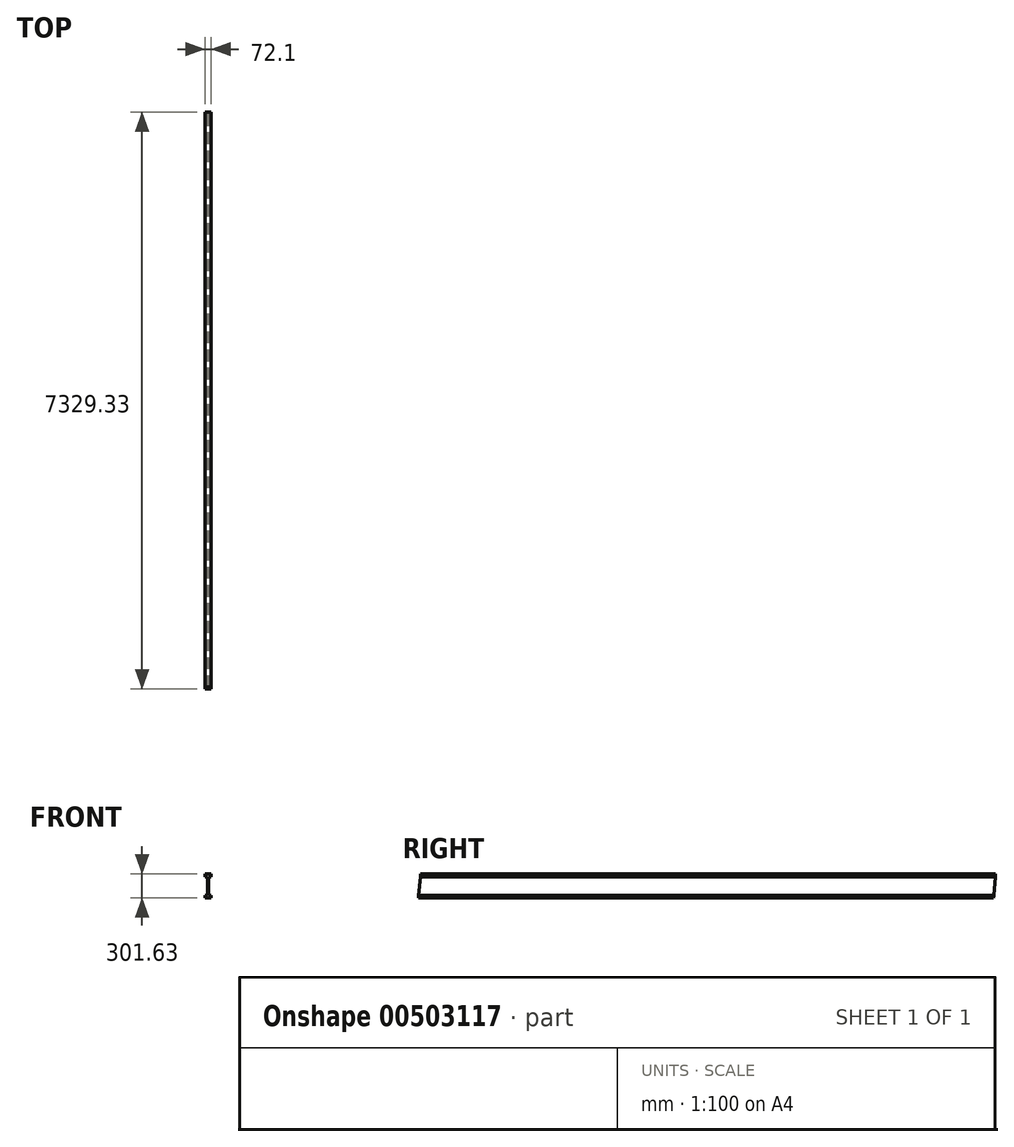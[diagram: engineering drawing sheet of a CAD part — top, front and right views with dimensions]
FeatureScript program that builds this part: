
annotation { "Feature Type Name" : "Feature", "Feature Type Description" : "" }
export const myFeature = defineFeature(function(context is Context, id is Id, definition is map)
    precondition{}
    {
        {
            var Q0;
            Q0=qCreatedBy(makeId("Front.planeOp"),FACE);
            var sketch = newSketch(context, id + "F0", { "sketchPlane" : qUnion([Q0])});
            skLineSegment(sketch, "E0", {"start": v(0, 0) * mm, "end": v(0, 33.65) * mm});
            skLineSegment(sketch, "E1", {"start": v(0, 33.65) * mm, "end": v(31.29, 33.65) * mm});
            skLineSegment(sketch, "E2", {"start": v(31.29, 33.65) * mm, "end": v(31.29, 267.97) * mm});
            skLineSegment(sketch, "E3", {"start": v(31.29, 267.97) * mm, "end": v(0, 267.97) * mm});
            skLineSegment(sketch, "E4", {"start": v(0, 267.97) * mm, "end": v(0, 301.63) * mm});
            skLineSegment(sketch, "E5", {"start": v(0, 301.63) * mm, "end": v(72.1, 301.63) * mm});
            skLineSegment(sketch, "E6", {"start": v(72.1, 301.63) * mm, "end": v(72.1, 267.97) * mm});
            skLineSegment(sketch, "E7", {"start": v(72.1, 267.97) * mm, "end": v(40.81, 267.97) * mm});
            skLineSegment(sketch, "E8", {"start": v(40.81, 267.97) * mm, "end": v(40.81, 33.65) * mm});
            skLineSegment(sketch, "E9", {"start": v(40.81, 33.65) * mm, "end": v(72.1, 33.66) * mm});
            skLineSegment(sketch, "E10", {"start": v(72.1, 33.66) * mm, "end": v(72.1, 0) * mm});
            skLineSegment(sketch, "E11", {"start": v(72.1, 0) * mm, "end": v(0, 0) * mm});
            skSolve(sketch);
        }
        {
            var Q0;
            Q0 = qSketchRegion(id + "F0", true);
            extrude(context, id + "F1", {"entities" : qUnion([Q0]), "depth" : 7620 * mm});
        }
        {
            var Q0;
            Q0=makeQuery(id+"F1.opExtrude","SWEPT_FACE",FACE,{"disambiguationData":[OSD([sQuery(id+"F0.wireOp",EDGE,"E10")])]});
            var sketch = newSketch(context, id + "F2", { "sketchPlane" : qUnion([Q0])});
            skLineSegment(sketch, "E12", {"start": v(-7620, 0) * mm, "end": v(-7594.25, 301.63) * mm});
            skLineSegment(sketch, "E13", {"start": v(-7620, 0) * mm, "end": v(-7620, 301.63) * mm});
            skLineSegment(sketch, "E14", {"start": v(-7620, 301.63) * mm, "end": v(-7594.25, 301.63) * mm});
            skSolve(sketch);
        }
        {
            var Q0;
            Q0 = qSketchRegion(id + "F2", true);
            extrude(context, id + "F3", {"entities" : qUnion([Q0]), "operationType" : NewBodyOperationType.REMOVE, "endBound" : BoundingType.THROUGH_ALL, "oppositeDirection" : true, "depth" : 25.4 * mm});
        }
        {
            var Q0;
            Q0=makeQuery(id+"F1.opExtrude","SWEPT_FACE",FACE,{"disambiguationData":[OSD([sQuery(id+"F0.wireOp",EDGE,"E0")])]});
            var sketch = newSketch(context, id + "F4", { "sketchPlane" : qUnion([Q0])});
            skLineSegment(sketch, "E15", {"start": v(316.42, 0) * mm, "end": v(290.67, 301.63) * mm});
            skLineSegment(sketch, "E16", {"start": v(290.67, 301.63) * mm, "end": v(0, 301.63) * mm});
            skLineSegment(sketch, "E17", {"start": v(0, 301.63) * mm, "end": v(0, 0) * mm});
            skLineSegment(sketch, "E18", {"start": v(0, 0) * mm, "end": v(316.42, 0) * mm});
            skSolve(sketch);
        }
        {
            var Q0;
            Q0 = qSketchRegion(id + "F4", true);
            extrude(context, id + "F5", {"entities" : qUnion([Q0]), "operationType" : NewBodyOperationType.REMOVE, "endBound" : BoundingType.THROUGH_ALL, "oppositeDirection" : true, "depth" : 25.4 * mm});
        }
    });
